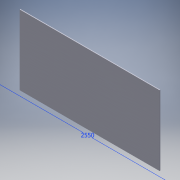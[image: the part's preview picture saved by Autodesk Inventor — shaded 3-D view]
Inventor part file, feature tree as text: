
AUTODESK INVENTOR PART (.ipt)
format: ipt  version: 2019 (Build 230136000, 136)  size: 98,304 bytes
history: native  units: mm
features: extrude x1, sketch x1
ambient origin geometry x8: Origin, YZ Plane, XZ Plane, XY Plane, X Axis, Y Axis, Z Axis, Center Point
bodies: Solid1 (feature_tree)
feature tree (2):
  extrude  "Extrusion1"  Depth=900.0mm
  sketch  "Sketch1"  dims[d0=2550.0mm d1=900.0mm d2=10.0mm d3=0.0mm]
